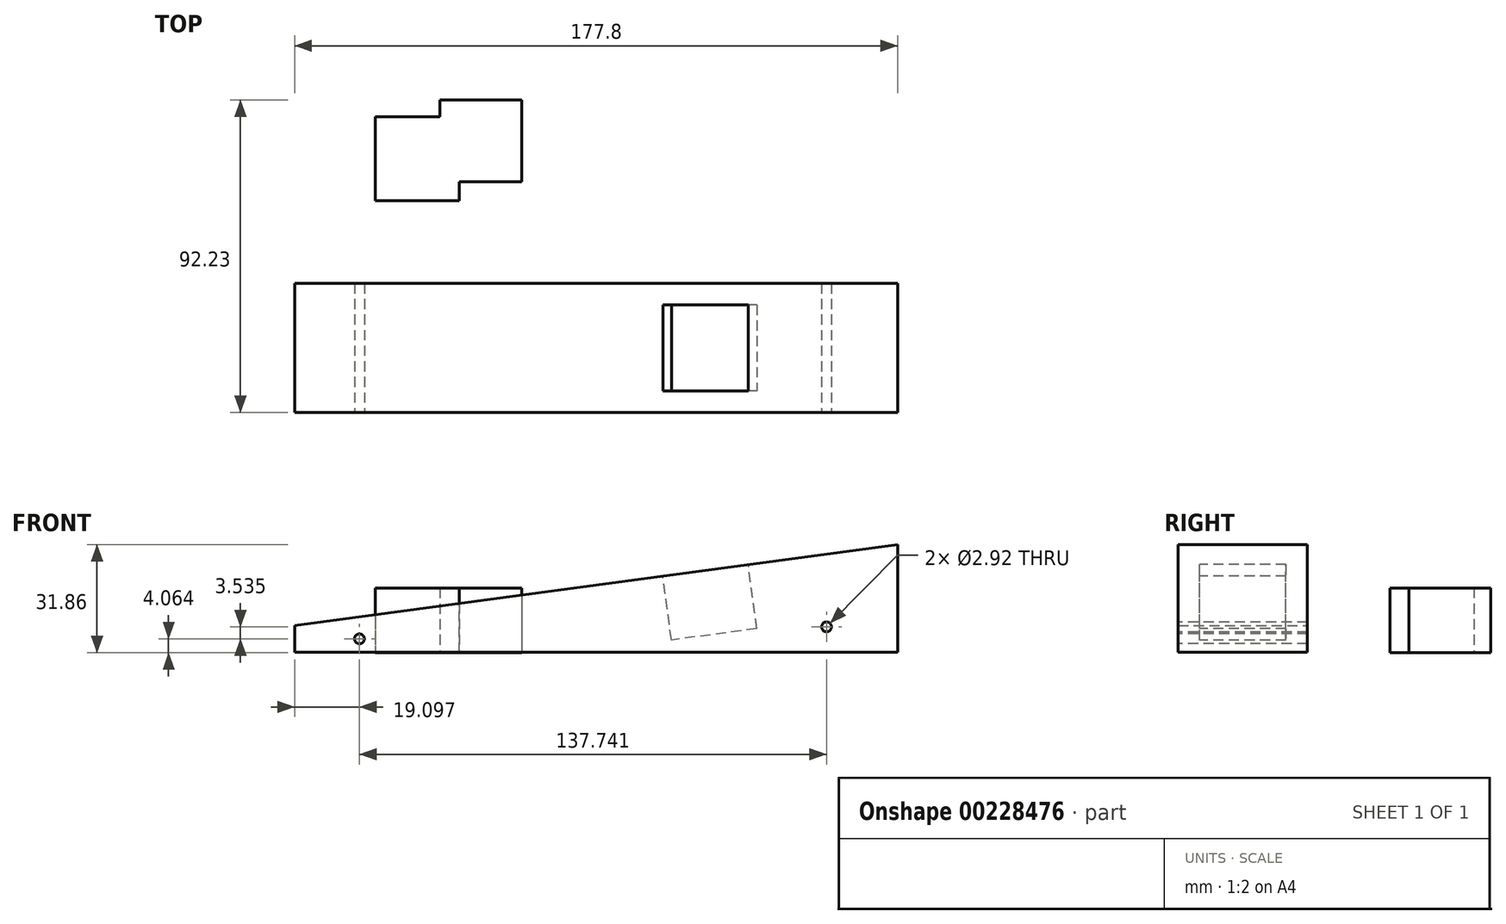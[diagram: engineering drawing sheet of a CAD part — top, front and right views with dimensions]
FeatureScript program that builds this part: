
annotation { "Feature Type Name" : "Feature", "Feature Type Description" : "" }
export const myFeature = defineFeature(function(context is Context, id is Id, definition is map)
    precondition{}
    {
        {
            var Q0;
            Q0=qCreatedBy(makeId("Front.planeOp"),FACE);
            var sketch = newSketch(context, id + "F0", { "sketchPlane" : qUnion([Q0])});
            skLineSegment(sketch, "E0", {"start": v(96.64, 31.86) * mm, "end": v(96.64, 0.1) * mm});
            skLineSegment(sketch, "E1", {"start": v(96.64, 0.1) * mm, "end": v(-81.16, 0.1) * mm});
            skLineSegment(sketch, "E2", {"start": v(-81.16, 0.1) * mm, "end": v(-81.16, 8.05) * mm});
            skLineSegment(sketch, "E3", {"start": v(-81.16, 8.05) * mm, "end": v(96.64, 31.86) * mm});
            skSolve(sketch);
        }
        {
            var Q0;
            Q0=makeQuery(id+"F0.imprint","IMPRINT",FACE,{"disambiguationData":[TD([[makeQuery(id+"F0.imprint","IMPRINT",EDGE,{"derivedFrom":sQuery(id+"F0.wireOp",EDGE,"E0")}),-1.0]])]});
            extrude(context, id + "F1", {"entities" : qUnion([Q0]), "depth" : 38.1 * mm});
        }
        {
            var Q0;
            Q0=makeQuery(id+"F1.opExtrude","SWEPT_FACE",FACE,{"disambiguationData":[OSD([sQuery(id+"F0.wireOp",EDGE,"E3")])]});
            var sketch = newSketch(context, id + "F2", { "sketchPlane" : qUnion([Q0])});
            skLineSegment(sketch, "E4", {"start": v(55.56, -6.35) * mm, "end": v(30.16, -6.35) * mm});
            skLineSegment(sketch, "E5", {"start": v(30.16, -6.35) * mm, "end": v(30.16, -31.75) * mm});
            skLineSegment(sketch, "E6", {"start": v(30.16, -31.75) * mm, "end": v(55.56, -31.75) * mm});
            skLineSegment(sketch, "E7", {"start": v(55.56, -6.35) * mm, "end": v(55.56, -31.75) * mm});
            skSolve(sketch);
        }
        {
            var Q0;
            Q0=makeQuery(id+"F1.opExtrude","CAP_FACE",FACE,{"disambiguationData":[OSD([sQuery(id+"F0.wireOp",EDGE,"E0"),sQuery(id+"F0.wireOp",EDGE,"E1"),sQuery(id+"F0.wireOp",EDGE,"E2"),sQuery(id+"F0.wireOp",EDGE,"E3")])],"isStart":false});
            var sketch = newSketch(context, id + "F3", { "sketchPlane" : qUnion([Q0])});
            skSolve(sketch);
        }
        {
            var Q0;
            Q0 = qSketchRegion(id + "F2", true);
            extrude(context, id + "F4", {"entities" : qUnion([Q0]), "operationType" : NewBodyOperationType.REMOVE, "oppositeDirection" : true, "depth" : 19.05 * mm});
        }
        {
            var Q0;
            Q0=makeQuery(id+"F3.imprint","IMPRINT",FACE,{"disambiguationData":[TD([[makeQuery(id+"F3.imprint","IMPRINT",EDGE,{"derivedFrom":makeQuery(id+"F1.opExtrude","CAP_EDGE",EDGE,{"disambiguationData":[OSD([sQuery(id+"F0.wireOp",EDGE,"E0")])],"isStart":false})}),-1.0]])]});
            var sketch = newSketch(context, id + "F5", { "sketchPlane" : qUnion([Q0])});
            skLineSegment(sketch, "E8", {"start": v(55.47, 0) * mm, "end": v(55.47, 4.06) * mm});
            skSolve(sketch);
        }
        {
            var Q0;
            Q0=makeQuery(id+"F5.imprint","IMPRINT",FACE,{"disambiguationData":[TD([[makeQuery(id+"F5.imprint","IMPRINT",EDGE,{"derivedFrom":makeQuery(id+"F3.imprint","IMPRINT",EDGE,{"derivedFrom":makeQuery(id+"F1.opExtrude","CAP_EDGE",EDGE,{"disambiguationData":[OSD([sQuery(id+"F0.wireOp",EDGE,"E0")])],"isStart":false})})}),-1.0]])]});
            var sketch = newSketch(context, id + "F6", { "sketchPlane" : qUnion([Q0])});
            skCircle(sketch, "E9", {"center": v(-62.06, 4.06) * mm, "radius": 1.46 * mm});
            skSolve(sketch);
        }
        {
            var Q0;
            Q0 = qSketchRegion(id + "F6", true);
            extrude(context, id + "F7", {"entities" : qUnion([Q0]), "operationType" : NewBodyOperationType.REMOVE, "oppositeDirection" : true, "depth" : 38.1 * mm});
        }
        {
            var Q0;
            Q0=qCreatedBy(makeId("Top.planeOp"),FACE);
            var sketch = newSketch(context, id + "F8", { "sketchPlane" : qUnion([Q0])});
            skLineSegment(sketch, "E10.bottom", {"start": v(-57.4, 49.1) * mm, "end": v(-32.64, 49.1) * mm});
            skLineSegment(sketch, "E10.top", {"start": v(-57.4, 24.33) * mm, "end": v(-32.64, 24.33) * mm});
            skLineSegment(sketch, "E10.left", {"start": v(-57.4, 49.1) * mm, "end": v(-57.4, 24.33) * mm});
            skLineSegment(sketch, "E10.right", {"start": v(-32.64, 49.1) * mm, "end": v(-32.64, 24.33) * mm});
            skSolve(sketch);
        }
        {
            var Q0;
            Q0=makeQuery(id+"F5.imprint","IMPRINT",FACE,{"disambiguationData":[TD([[makeQuery(id+"F5.imprint","IMPRINT",EDGE,{"derivedFrom":makeQuery(id+"F3.imprint","IMPRINT",EDGE,{"derivedFrom":makeQuery(id+"F1.opExtrude","CAP_EDGE",EDGE,{"disambiguationData":[OSD([sQuery(id+"F0.wireOp",EDGE,"E0")])],"isStart":false})})}),-1.0]])]});
            var sketch = newSketch(context, id + "F9", { "sketchPlane" : qUnion([Q0])});
            skCircle(sketch, "E11", {"center": v(75.68, 7.6) * mm, "radius": 1.46 * mm});
            skSolve(sketch);
        }
        {
            var Q0;
            Q0 = qSketchRegion(id + "F9", true);
            extrude(context, id + "F10", {"entities" : qUnion([Q0]), "operationType" : NewBodyOperationType.REMOVE, "oppositeDirection" : true, "depth" : 38.1 * mm});
        }
        {
            var Q0;
            Q0=makeQuery(id+"F8.imprint","IMPRINT",FACE,{"disambiguationData":[TD([[makeQuery(id+"F8.imprint","IMPRINT",EDGE,{"derivedFrom":sQuery(id+"F8.wireOp",EDGE,"E10.bottom")}),-1.0]])]});
            extrude(context, id + "F11", {"entities" : qUnion([Q0]), "operationType" : NewBodyOperationType.ADD, "depth" : 19.05 * mm});
        }
        {
            var Q0;
            Q0=qCreatedBy(makeId("Top.planeOp"),FACE);
            var sketch = newSketch(context, id + "F12", { "sketchPlane" : qUnion([Q0])});
            skLineSegment(sketch, "E12.bottom", {"start": v(-38.35, 54.13) * mm, "end": v(-14.22, 54.13) * mm});
            skLineSegment(sketch, "E12.top", {"start": v(-38.35, 30) * mm, "end": v(-14.22, 30) * mm});
            skLineSegment(sketch, "E12.left", {"start": v(-38.35, 54.13) * mm, "end": v(-38.35, 30) * mm});
            skLineSegment(sketch, "E12.right", {"start": v(-14.22, 54.13) * mm, "end": v(-14.22, 30) * mm});
            skSolve(sketch);
        }
        {
            var Q0;
            Q0=makeQuery(id+"F12.imprint","IMPRINT",FACE,{"disambiguationData":[TD([[makeQuery(id+"F12.imprint","IMPRINT",EDGE,{"derivedFrom":sQuery(id+"F12.wireOp",EDGE,"E12.bottom")}),-1.0]])]});
            extrude(context, id + "F13", {"entities" : qUnion([Q0]), "operationType" : NewBodyOperationType.ADD, "depth" : 19.05 * mm});
        }
    });
